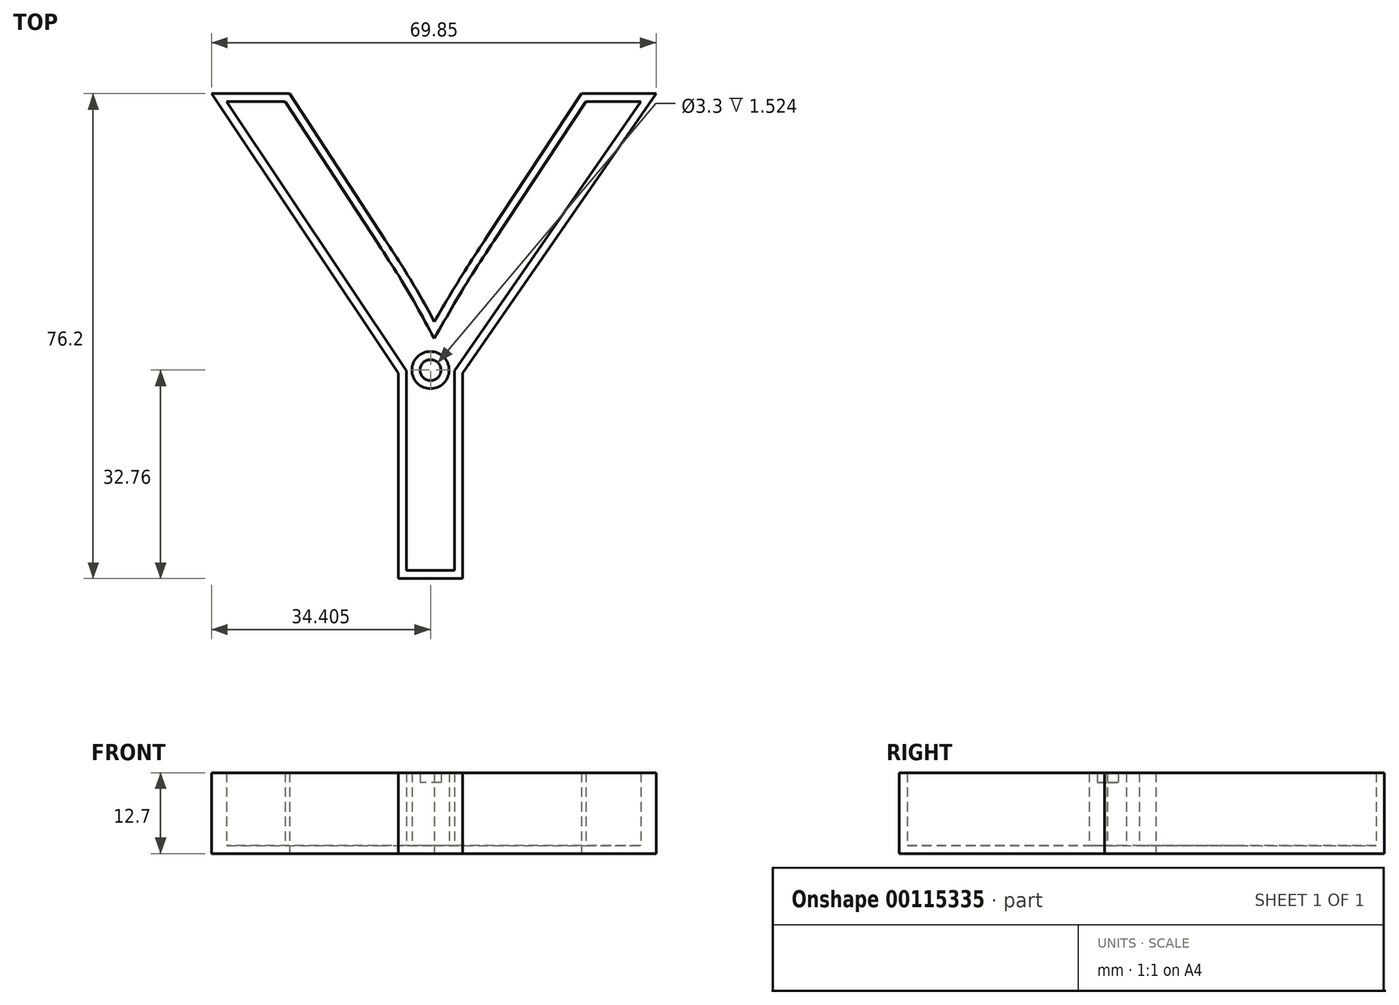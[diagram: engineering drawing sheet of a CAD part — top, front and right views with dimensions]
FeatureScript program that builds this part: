
annotation { "Feature Type Name" : "Feature", "Feature Type Description" : "" }
export const myFeature = defineFeature(function(context is Context, id is Id, definition is map)
    precondition{}
    {
        {
            var Q0;
            Q0=qCreatedBy(makeId("Top.planeOp"),FACE);
            var sketch = newSketch(context, id + "F0", { "sketchPlane" : qUnion([Q0])});
            skFitSpline(sketch, "E0", {"points": [v(-7.7, 18.2) * mm, v(-4.93, 13.9) * mm, v(-2.35, 9.6) * mm, v(0.04, 5.3) * mm]});
            skFitSpline(sketch, "E1", {"points": [v(0.04, 5.3) * mm, v(2.33, 9.3) * mm, v(5.1, 13.78) * mm, v(8.36, 18.77) * mm]});
            skLineSegment(sketch, "E2", {"start": v(-5.63, -35.03) * mm, "end": v(-5.63, -2.75) * mm});
            skLineSegment(sketch, "E3", {"start": v(-5.63, -2.75) * mm, "end": v(-35, 41.17) * mm});
            skLineSegment(sketch, "E4", {"start": v(-35, 41.17) * mm, "end": v(-22.73, 41.17) * mm});
            skLineSegment(sketch, "E5", {"start": v(-22.73, 41.17) * mm, "end": v(-7.7, 18.2) * mm});
            skLineSegment(sketch, "E6", {"start": v(8.36, 18.77) * mm, "end": v(23.12, 41.17) * mm});
            skLineSegment(sketch, "E7", {"start": v(23.12, 41.17) * mm, "end": v(34.86, 41.17) * mm});
            skLineSegment(sketch, "E8", {"start": v(34.86, 41.17) * mm, "end": v(4.46, -2.75) * mm});
            skLineSegment(sketch, "E9", {"start": v(4.46, -2.75) * mm, "end": v(4.46, -35.03) * mm});
            skLineSegment(sketch, "E10", {"start": v(4.46, -35.03) * mm, "end": v(-5.63, -35.03) * mm});
            skSolve(sketch);
        }
        {
            var Q0;
            Q0 = qSketchRegion(id + "F0", true);
            extrude(context, id + "F1", {"entities" : qUnion([Q0]), "depth" : 12.7 * mm});
        }
        {
            var Q0;
            Q0=makeQuery(id+"F1.opExtrude","CAP_FACE",FACE,{"disambiguationData":[OSD([sQuery(id+"F0.wireOp",EDGE,"E0"),sQuery(id+"F0.wireOp",EDGE,"E1"),sQuery(id+"F0.wireOp",EDGE,"E2"),sQuery(id+"F0.wireOp",EDGE,"E3"),sQuery(id+"F0.wireOp",EDGE,"E4"),sQuery(id+"F0.wireOp",EDGE,"E5"),sQuery(id+"F0.wireOp",EDGE,"E6"),sQuery(id+"F0.wireOp",EDGE,"E7"),sQuery(id+"F0.wireOp",EDGE,"E8"),sQuery(id+"F0.wireOp",EDGE,"E9"),sQuery(id+"F0.wireOp",EDGE,"E10")])],"isStart":false});
            shell(context, id + "F2", {"entities" : qUnion([Q0]), "thickness" : 1.27 * mm});
        }
        {
            var Q0;
            Q0=makeQuery(id+"F2.opShell","OFFSET_FACE",FACE,{"disambiguationData":[OSD([sQuery(id+"F0.wireOp",EDGE,"E0"),sQuery(id+"F0.wireOp",EDGE,"E1"),sQuery(id+"F0.wireOp",EDGE,"E2"),sQuery(id+"F0.wireOp",EDGE,"E3"),sQuery(id+"F0.wireOp",EDGE,"E4"),sQuery(id+"F0.wireOp",EDGE,"E5"),sQuery(id+"F0.wireOp",EDGE,"E6"),sQuery(id+"F0.wireOp",EDGE,"E7"),sQuery(id+"F0.wireOp",EDGE,"E8"),sQuery(id+"F0.wireOp",EDGE,"E9"),sQuery(id+"F0.wireOp",EDGE,"E10")])]});
            var sketch = newSketch(context, id + "F3", { "sketchPlane" : qUnion([Q0])});
            skPoint(sketch, "E11.first.point", {"position": v(-4.36, -2.36) * mm});
            skPoint(sketch, "E11.second.point", {"position": v(3.19, -2.35) * mm});
            skPoint(sketch, "E11.third.point", {"position": v(0, 1.46) * mm});
            skCircle(sketch, "E12", {"center": v(-0.58, -2.27) * mm, "radius": 1.65 * mm});
            skCircle(sketch, "E13", {"center": v(-0.58, -2.27) * mm, "radius": 2.92 * mm});
            skSolve(sketch);
        }
        {
            var Q0;
            Q0=makeQuery(id+"F3.imprint","IMPRINT",FACE,{"disambiguationData":[TD([[makeQuery(id+"F3.imprint","IMPRINT",EDGE,{"derivedFrom":sQuery(id+"F3.wireOp",EDGE,"E12")}),-1.0]])]});
            extrude(context, id + "F4", {"entities" : qUnion([Q0]), "operationType" : NewBodyOperationType.ADD, "depth" : 11.43 * mm});
        }
        {
            var Q0;
            Q0=makeQuery(id+"F4.boolean.opBoolean","SPLIT",FACE,{"disambiguationData":[TD([makeQuery(id+"F4.opExtrude","SWEPT_FACE",FACE,{"disambiguationData":[OSD([sQuery(id+"F3.wireOp",EDGE,"E12")])]})])],"derivedFrom":makeQuery(id+"F2.opShell","OFFSET_FACE",FACE,{"disambiguationData":[OSD([sQuery(id+"F0.wireOp",EDGE,"E0"),sQuery(id+"F0.wireOp",EDGE,"E1"),sQuery(id+"F0.wireOp",EDGE,"E2"),sQuery(id+"F0.wireOp",EDGE,"E3"),sQuery(id+"F0.wireOp",EDGE,"E4"),sQuery(id+"F0.wireOp",EDGE,"E5"),sQuery(id+"F0.wireOp",EDGE,"E6"),sQuery(id+"F0.wireOp",EDGE,"E7"),sQuery(id+"F0.wireOp",EDGE,"E8"),sQuery(id+"F0.wireOp",EDGE,"E9"),sQuery(id+"F0.wireOp",EDGE,"E10")])]})});
            extrude(context, id + "F5", {"entities" : qUnion([Q0]), "operationType" : NewBodyOperationType.ADD, "depth" : 9.9 * mm});
        }
    });
